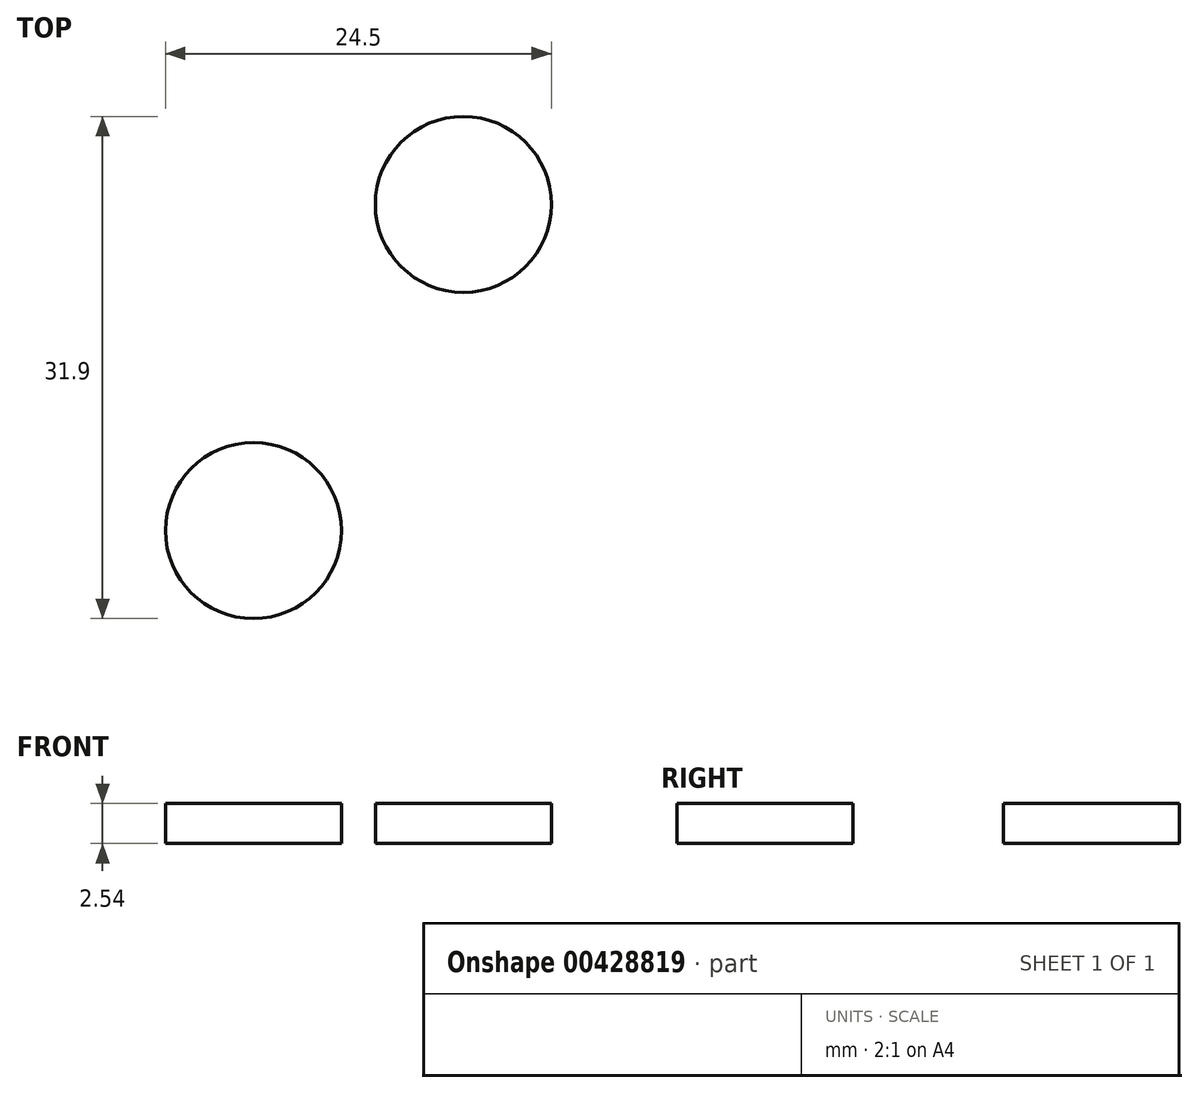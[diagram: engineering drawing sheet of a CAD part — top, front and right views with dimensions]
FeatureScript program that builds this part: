
annotation { "Feature Type Name" : "Feature", "Feature Type Description" : "" }
export const myFeature = defineFeature(function(context is Context, id is Id, definition is map)
    precondition{}
    {
        {
            var Q0;
            Q0=qCreatedBy(makeId("Top.planeOp"),FACE);
            var sketch = newSketch(context, id + "F0", { "sketchPlane" : qUnion([Q0])});
            skLineSegment(sketch, "E0", {"start": v(0, -6.35) * mm, "end": v(0, -86.36) * mm});
            skLineSegment(sketch, "E1", {"start": v(6.35, 0) * mm, "end": v(86.36, 0) * mm});
            skArc(sketch, "E2", {"start": v(9.08, -92.1) * mm, "mid": v(57.72, -57.72) * mm, "end": v(92.1, -9.08) * mm});
            skPoint(sketch, "E3.visualSharp", {"position": v(0, 0) * mm});
            skArc(sketch, "E3.filletArc", {"start": v(6.35, 0) * mm, "mid": v(1.86, -1.86) * mm, "end": v(0, -6.35) * mm});
            skPoint(sketch, "E4.visualSharp", {"position": v(96.11, 0) * mm});
            skArc(sketch, "E4.filletArc", {"start": v(92.1, -9.08) * mm, "mid": v(91.73, -2.96) * mm, "end": v(86.36, 0) * mm});
            skPoint(sketch, "E5.visualSharp", {"position": v(0, -96.11) * mm});
            skArc(sketch, "E5.filletArc", {"start": v(0, -86.36) * mm, "mid": v(2.96, -91.73) * mm, "end": v(9.08, -92.1) * mm});
            skLineSegment(sketch, "E6", {"start": v(-6.67, -92.7) * mm, "end": v(14.05, -92.7) * mm, "construction": true});
            skLineSegment(sketch, "E7", {"start": v(92.7, -25) * mm, "end": v(92.7, 15.7) * mm, "construction": true});
            skLineSegment(sketch, "E8", {"start": v(57.72, -57.72) * mm, "end": v(4.94, -110.49) * mm, "construction": true});
            skLineSegment(sketch, "E9", {"start": v(1.86, -1.86) * mm, "end": v(-52.37, -56.1) * mm, "construction": true});
            skArc(sketch, "E10.0", {"start": v(9.62, -91.27) * mm, "mid": v(57.36, -57.36) * mm, "end": v(91.27, -9.62) * mm});
            skLineSegment(sketch, "E10.1", {"start": v(0.5, -6.86) * mm, "end": v(0.5, -85.55) * mm});
            skLineSegment(sketch, "E10.2", {"start": v(6.86, -0.5) * mm, "end": v(85.55, -0.5) * mm});
            skPoint(sketch, "E11.visualSharp", {"position": v(0.5, -95.36) * mm});
            skArc(sketch, "E11.filletArc", {"start": v(0.5, -85.55) * mm, "mid": v(3.48, -90.93) * mm, "end": v(9.62, -91.27) * mm});
            skPoint(sketch, "E12.visualSharp", {"position": v(95.36, -0.5) * mm});
            skArc(sketch, "E12.filletArc", {"start": v(91.27, -9.62) * mm, "mid": v(90.93, -3.48) * mm, "end": v(85.55, -0.5) * mm});
            skPoint(sketch, "E13.visualSharp", {"position": v(0.5, -0.5) * mm});
            skArc(sketch, "E13.filletArc", {"start": v(6.86, -0.5) * mm, "mid": v(2.37, -2.37) * mm, "end": v(0.5, -6.86) * mm});
            skArc(sketch, "E14.0", {"start": v(8.51, -88.98) * mm, "mid": v(55.56, -55.56) * mm, "end": v(88.98, -8.51) * mm});
            skLineSegment(sketch, "E15.0", {"start": v(3.05, -6.86) * mm, "end": v(3.05, -85.55) * mm});
            skLineSegment(sketch, "E16.0", {"start": v(6.86, -3.05) * mm, "end": v(85.55, -3.05) * mm});
            skArc(sketch, "E17", {"start": v(3.05, -85.55) * mm, "mid": v(4.83, -88.78) * mm, "end": v(8.51, -88.98) * mm});
            skArc(sketch, "E18", {"start": v(88.98, -8.51) * mm, "mid": v(88.78, -4.83) * mm, "end": v(85.55, -3.05) * mm});
            skArc(sketch, "E19", {"start": v(6.86, -3.05) * mm, "mid": v(4.16, -4.16) * mm, "end": v(3.05, -6.86) * mm});
            skSolve(sketch);
        }
        {
            var Q0;
            Q0=makeQuery(id+"F0.imprint","IMPRINT",FACE,{"disambiguationData":[TD([[makeQuery(id+"F0.imprint","IMPRINT",EDGE,{"derivedFrom":sQuery(id+"F0.wireOp",EDGE,"E10.0")}),1.0]])]});
            extrude(context, id + "F1", {"entities" : qUnion([Q0]), "depth" : 12.7 * mm});
        }
        {
            var Q0;
            Q0=makeQuery(id+"F1.opExtrude","CAP_FACE",FACE,{"disambiguationData":[OSD([sQuery(id+"F0.wireOp",EDGE,"E10.0"),sQuery(id+"F0.wireOp",EDGE,"E10.1"),sQuery(id+"F0.wireOp",EDGE,"E10.2"),sQuery(id+"F0.wireOp",EDGE,"E11.filletArc"),sQuery(id+"F0.wireOp",EDGE,"E12.filletArc"),sQuery(id+"F0.wireOp",EDGE,"E13.filletArc"),sQuery(id+"F0.wireOp",EDGE,"E14.0"),sQuery(id+"F0.wireOp",EDGE,"E15.0"),sQuery(id+"F0.wireOp",EDGE,"E16.0"),sQuery(id+"F0.wireOp",EDGE,"E17"),sQuery(id+"F0.wireOp",EDGE,"E18"),sQuery(id+"F0.wireOp",EDGE,"E19")])],"isStart":false});
            var sketch = newSketch(context, id + "F2", { "sketchPlane" : qUnion([Q0])});
            skLineSegment(sketch, "E20.0", {"start": v(6.86, -0.5) * mm, "end": v(85.55, -0.5) * mm, "construction": true});
            skArc(sketch, "E21.0", {"start": v(6.86, -0.5) * mm, "mid": v(2.37, -2.37) * mm, "end": v(0.5, -6.86) * mm, "construction": true});
            skLineSegment(sketch, "E22.0", {"start": v(0.5, -6.86) * mm, "end": v(0.5, -85.55) * mm, "construction": true});
            skArc(sketch, "E23.0", {"start": v(0.5, -85.55) * mm, "mid": v(3.48, -90.93) * mm, "end": v(9.62, -91.27) * mm, "construction": true});
            skArc(sketch, "E24.0", {"start": v(9.62, -91.27) * mm, "mid": v(57.36, -57.36) * mm, "end": v(91.27, -9.62) * mm, "construction": true});
            skArc(sketch, "E25.0", {"start": v(91.27, -9.62) * mm, "mid": v(90.93, -3.48) * mm, "end": v(85.55, -0.5) * mm, "construction": true});
            skLineSegment(sketch, "E26.0", {"start": v(6.86, 5.84) * mm, "end": v(85.55, 5.84) * mm});
            skLineSegment(sketch, "E26.1", {"start": v(-5.84, -6.86) * mm, "end": v(-5.84, -85.55) * mm});
            skArc(sketch, "E26.2", {"start": v(-5.84, -85.55) * mm, "mid": v(0.1, -96.3) * mm, "end": v(12.38, -96.99) * mm});
            skArc(sketch, "E26.3", {"start": v(6.86, 5.84) * mm, "mid": v(-2.12, 2.12) * mm, "end": v(-5.84, -6.86) * mm});
            skArc(sketch, "E26.4", {"start": v(12.38, -96.99) * mm, "mid": v(61.85, -61.85) * mm, "end": v(96.99, -12.38) * mm});
            skArc(sketch, "E26.5", {"start": v(96.99, -12.38) * mm, "mid": v(96.3, -0.1) * mm, "end": v(85.55, 5.84) * mm});
            skSolve(sketch);
        }
        {
            var Q0;
            Q0=makeQuery(id+"F2.imprint","IMPRINT",FACE,{"disambiguationData":[TD([[makeQuery(id+"F2.imprint","IMPRINT",EDGE,{"derivedFrom":sQuery(id+"F2.wireOp",EDGE,"E26.0")}),-1.0]])]});
            var Q1;
            Q1=makeQuery(id+"F2.imprint","IMPRINT",FACE,{"disambiguationData":[TD([[makeQuery(id+"F2.imprint","IMPRINT",EDGE,{"derivedFrom":makeQuery(id+"F1.opExtrude","CAP_EDGE",EDGE,{"disambiguationData":[OSD([sQuery(id+"F0.wireOp",EDGE,"E14.0")])],"isStart":false})}),1.0]])]});
            var Q2;
            Q2=makeQuery(id+"F2.imprint","IMPRINT",FACE,{"disambiguationData":[TD([[makeQuery(id+"F2.imprint","IMPRINT",EDGE,{"derivedFrom":makeQuery(id+"F1.opExtrude","CAP_EDGE",EDGE,{"disambiguationData":[OSD([sQuery(id+"F0.wireOp",EDGE,"E10.0")])],"isStart":false})}),1.0]])]});
            extrude(context, id + "F3", {"entities" : qUnion([Q0, Q1, Q2]), "operationType" : NewBodyOperationType.ADD, "depth" : 2.54 * mm});
        }
        {
            var Q0;
            Q0=makeQuery(id+"F3.opExtrude","CAP_FACE",FACE,{"disambiguationData":[OSD([sQuery(id+"F2.wireOp",EDGE,"E26.0"),sQuery(id+"F2.wireOp",EDGE,"E26.1"),sQuery(id+"F2.wireOp",EDGE,"E26.2"),sQuery(id+"F2.wireOp",EDGE,"E26.3"),sQuery(id+"F2.wireOp",EDGE,"E26.4"),sQuery(id+"F2.wireOp",EDGE,"E26.5")])],"isStart":false});
            var sketch = newSketch(context, id + "F4", { "sketchPlane" : qUnion([Q0])});
            skArc(sketch, "E27.0", {"start": v(9.62, -91.27) * mm, "mid": v(57.36, -57.36) * mm, "end": v(91.27, -9.62) * mm});
            skArc(sketch, "E28.0.0", {"start": v(12.38, -96.99) * mm, "mid": v(0.1, -96.3) * mm, "end": v(-5.84, -85.55) * mm});
            skLineSegment(sketch, "E28.0.1", {"start": v(-5.84, -85.55) * mm, "end": v(-5.84, -6.86) * mm});
            skArc(sketch, "E28.0.2", {"start": v(-5.84, -6.86) * mm, "mid": v(-2.12, 2.12) * mm, "end": v(6.86, 5.84) * mm});
            skLineSegment(sketch, "E28.0.3", {"start": v(6.86, 5.84) * mm, "end": v(85.55, 5.84) * mm});
            skArc(sketch, "E28.0.4", {"start": v(85.55, 5.84) * mm, "mid": v(96.3, -0.1) * mm, "end": v(96.99, -12.38) * mm});
            skArc(sketch, "E28.0.5", {"start": v(96.99, -12.38) * mm, "mid": v(61.85, -61.85) * mm, "end": v(12.38, -96.99) * mm});
            skLineSegment(sketch, "E29", {"start": v(0, 0) * mm, "end": v(61.85, -61.85) * mm, "construction": true});
            skArc(sketch, "E30.0", {"start": v(79.32, -5.15) * mm, "mid": v(48.38, -48.38) * mm, "end": v(5.15, -79.32) * mm, "construction": true});
            skCircle(sketch, "E31", {"center": v(48.38, -48.38) * mm, "radius": 5.59 * mm});
            skCircle(sketch, "E32", {"center": v(31.46, -63.1) * mm, "radius": 5.59 * mm});
            skCircle(sketch, "E33", {"center": v(10.74, -76.43) * mm, "radius": 5.59 * mm});
            skLineSegment(sketch, "E34", {"start": v(0, 0) * mm, "end": v(10.74, -76.43) * mm, "construction": true});
            skLineSegment(sketch, "E35", {"start": v(0, 0) * mm, "end": v(0, -86.63) * mm, "construction": true});
            skLineSegment(sketch, "E36", {"start": v(0, 0) * mm, "end": v(31.46, -63.1) * mm, "construction": true});
            skCircle(sketch, "E37.MirrorC", {"center": v(63.1, -31.46) * mm, "radius": 5.59 * mm});
            skCircle(sketch, "E38.MirrorC", {"center": v(76.43, -10.74) * mm, "radius": 5.59 * mm});
            skLineSegment(sketch, "E39", {"start": v(76.43, -10.74) * mm, "end": v(10.74, -10.74) * mm, "construction": true});
            skLineSegment(sketch, "E40", {"start": v(10.74, -76.43) * mm, "end": v(10.74, -10.74) * mm, "construction": true});
            skCircle(sketch, "E41", {"center": v(10.74, -10.74) * mm, "radius": 5.59 * mm});
            skCircle(sketch, "E42", {"center": v(10.74, -43.59) * mm, "radius": 5.59 * mm});
            skCircle(sketch, "E43", {"center": v(43.59, -10.74) * mm, "radius": 5.59 * mm});
            skCircle(sketch, "E44", {"center": v(30.92, -30.92) * mm, "radius": 8.76 * mm});
            skSolve(sketch);
        }
        {
            var Q0;
            Q0=makeQuery(id+"F4.imprint","IMPRINT",FACE,{"disambiguationData":[TD([[makeQuery(id+"F4.imprint","IMPRINT",EDGE,{"derivedFrom":sQuery(id+"F4.wireOp",EDGE,"E41")}),1.0]])]});
            var Q1;
            Q1=makeQuery(id+"F4.imprint","IMPRINT",FACE,{"disambiguationData":[TD([[makeQuery(id+"F4.imprint","IMPRINT",EDGE,{"derivedFrom":sQuery(id+"F4.wireOp",EDGE,"E44")}),1.0]])]});
            var Q2;
            Q2=makeQuery(id+"F4.imprint","IMPRINT",FACE,{"disambiguationData":[TD([[makeQuery(id+"F4.imprint","IMPRINT",EDGE,{"derivedFrom":sQuery(id+"F4.wireOp",EDGE,"E43")}),1.0]])]});
            var Q3;
            Q3=makeQuery(id+"F4.imprint","IMPRINT",FACE,{"disambiguationData":[TD([[makeQuery(id+"F4.imprint","IMPRINT",EDGE,{"derivedFrom":sQuery(id+"F4.wireOp",EDGE,"E42")}),1.0]])]});
            var Q4;
            Q4=makeQuery(id+"F4.imprint","IMPRINT",FACE,{"disambiguationData":[TD([[makeQuery(id+"F4.imprint","IMPRINT",EDGE,{"derivedFrom":sQuery(id+"F4.wireOp",EDGE,"E33")}),1.0]])]});
            var Q5;
            Q5=makeQuery(id+"F4.imprint","IMPRINT",FACE,{"disambiguationData":[TD([[makeQuery(id+"F4.imprint","IMPRINT",EDGE,{"derivedFrom":sQuery(id+"F4.wireOp",EDGE,"E32")}),1.0]])]});
            var Q6;
            Q6=makeQuery(id+"F4.imprint","IMPRINT",FACE,{"disambiguationData":[TD([[makeQuery(id+"F4.imprint","IMPRINT",EDGE,{"derivedFrom":sQuery(id+"F4.wireOp",EDGE,"E31")}),1.0]])]});
            var Q7;
            Q7=makeQuery(id+"F4.imprint","IMPRINT",FACE,{"disambiguationData":[TD([[makeQuery(id+"F4.imprint","IMPRINT",EDGE,{"derivedFrom":sQuery(id+"F4.wireOp",EDGE,"E37.MirrorC")}),-1.0]])]});
            var Q8;
            Q8=makeQuery(id+"F4.imprint","IMPRINT",FACE,{"disambiguationData":[TD([[makeQuery(id+"F4.imprint","IMPRINT",EDGE,{"derivedFrom":sQuery(id+"F4.wireOp",EDGE,"E38.MirrorC")}),-1.0]])]});
            extrude(context, id + "F5", {"entities" : qUnion([Q0, Q1, Q2, Q3, Q4, Q5, Q6, Q7, Q8]), "operationType" : NewBodyOperationType.REMOVE, "oppositeDirection" : true, "depth" : 25.4 * mm});
        }
    });
